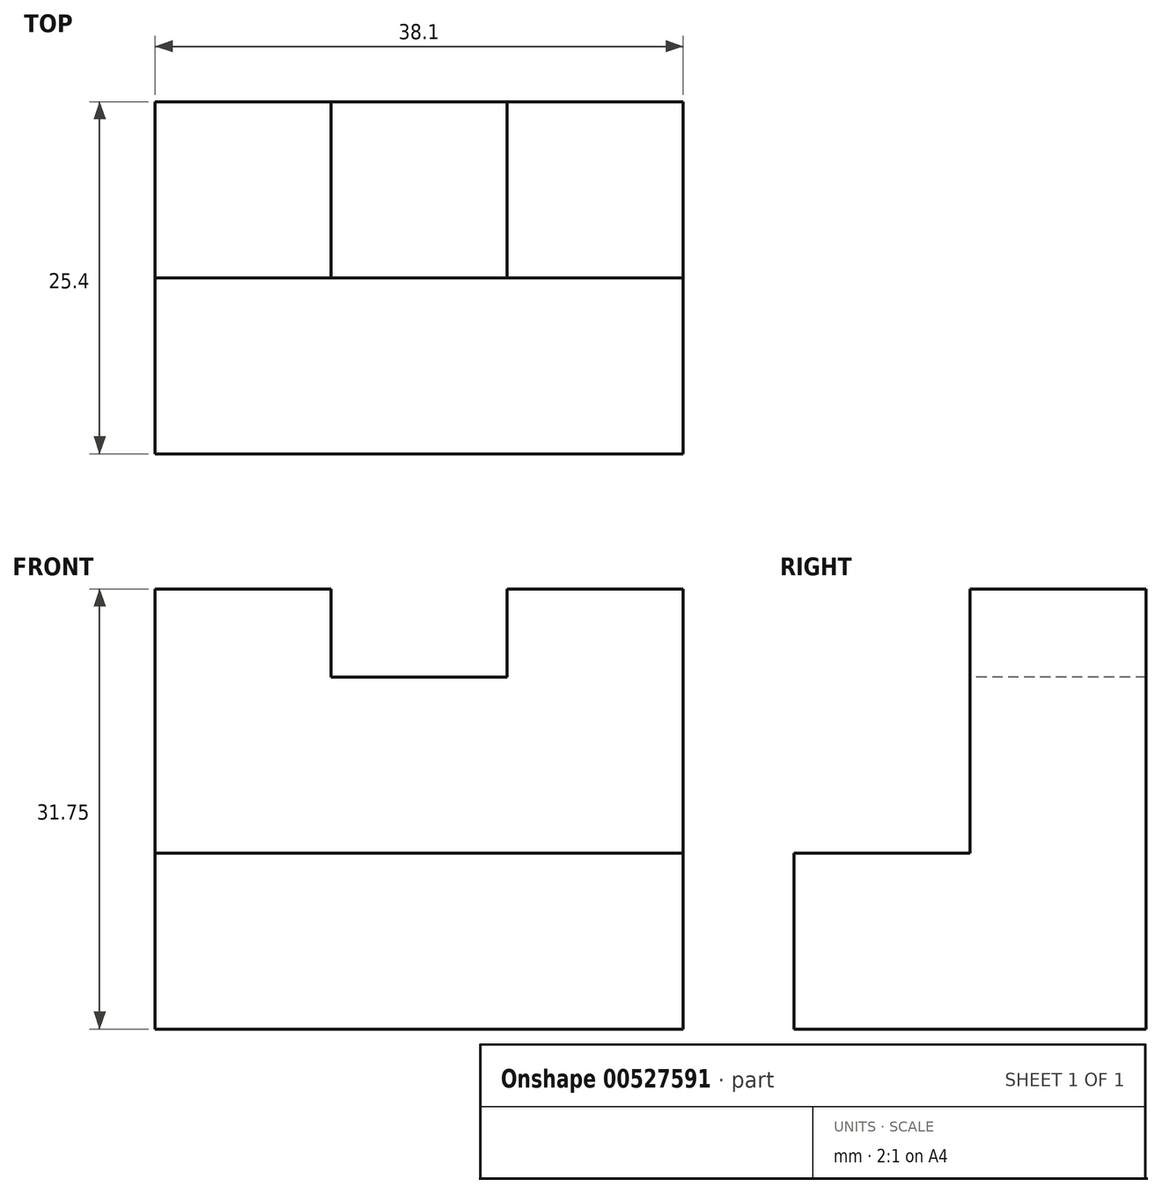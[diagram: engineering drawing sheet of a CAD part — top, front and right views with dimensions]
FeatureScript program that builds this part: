
annotation { "Feature Type Name" : "Feature", "Feature Type Description" : "" }
export const myFeature = defineFeature(function(context is Context, id is Id, definition is map)
    precondition{}
    {
        {
            var Q0;
            Q0=qCreatedBy(makeId("Right.planeOp"),FACE);
            var sketch = newSketch(context, id + "F0", { "sketchPlane" : qUnion([Q0])});
            skLineSegment(sketch, "E0", {"start": v(0, 0) * mm, "end": v(25.4, 0) * mm});
            skLineSegment(sketch, "E1", {"start": v(25.4, 0) * mm, "end": v(25.4, 31.75) * mm});
            skLineSegment(sketch, "E2", {"start": v(25.4, 31.75) * mm, "end": v(12.7, 31.75) * mm});
            skLineSegment(sketch, "E3", {"start": v(12.7, 31.75) * mm, "end": v(12.7, 12.7) * mm});
            skLineSegment(sketch, "E4", {"start": v(12.7, 12.7) * mm, "end": v(0, 12.7) * mm});
            skLineSegment(sketch, "E5", {"start": v(0, 12.7) * mm, "end": v(0, 0) * mm});
            skSolve(sketch);
        }
        {
            var Q0;
            Q0=makeQuery(id+"F0.imprint","IMPRINT",FACE,{"disambiguationData":[TD([[makeQuery(id+"F0.imprint","IMPRINT",EDGE,{"derivedFrom":sQuery(id+"F0.wireOp",EDGE,"E0")}),1.0]])]});
            extrude(context, id + "F1", {"entities" : qUnion([Q0]), "depth" : 38.1 * mm, "offsetDistance" : 25.4 * mm});
        }
        {
            var Q0;
            Q0=makeQuery(id+"F1.opExtrude","SWEPT_FACE",FACE,{"disambiguationData":[OSD([sQuery(id+"F0.wireOp",EDGE,"E3")])]});
            var sketch = newSketch(context, id + "F2", { "sketchPlane" : qUnion([Q0])});
            skLineSegment(sketch, "E6", {"start": v(38.1, 31.75) * mm, "end": v(25.4, 31.75) * mm});
            skLineSegment(sketch, "E7", {"start": v(25.4, 31.75) * mm, "end": v(25.4, 25.4) * mm});
            skLineSegment(sketch, "E8", {"start": v(25.4, 25.4) * mm, "end": v(12.7, 25.4) * mm});
            skLineSegment(sketch, "E9", {"start": v(12.7, 25.4) * mm, "end": v(12.7, 31.75) * mm});
            skLineSegment(sketch, "E10", {"start": v(12.7, 31.75) * mm, "end": v(0, 31.75) * mm});
            skLineSegment(sketch, "E11", {"start": v(12.7, 31.75) * mm, "end": v(25.4, 31.75) * mm});
            skSolve(sketch);
        }
        {
            var Q0;
            Q0=makeQuery(id+"F2.imprint","IMPRINT",FACE,{"disambiguationData":[TD([[makeQuery(id+"F2.imprint","IMPRINT",EDGE,{"derivedFrom":sQuery(id+"F2.wireOp",EDGE,"E7")}),-1.0]])]});
            extrude(context, id + "F3", {"entities" : qUnion([Q0]), "operationType" : NewBodyOperationType.REMOVE, "oppositeDirection" : true, "depth" : 12.7 * mm, "offsetDistance" : 25.4 * mm});
        }
    });
